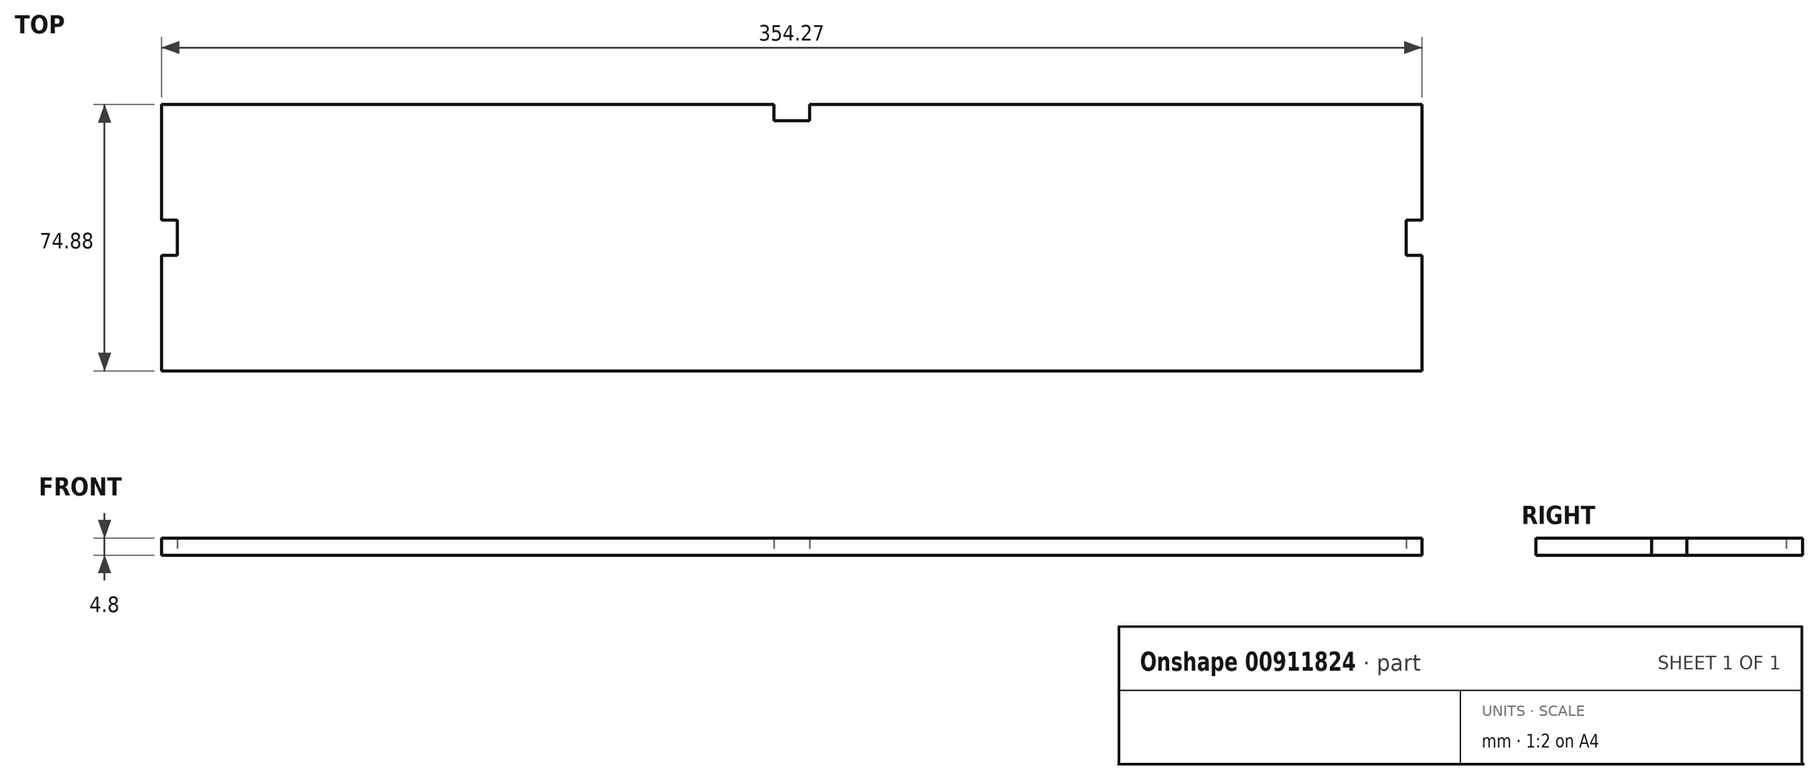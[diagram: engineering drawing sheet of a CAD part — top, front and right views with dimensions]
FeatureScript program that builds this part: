
annotation { "Feature Type Name" : "Feature", "Feature Type Description" : "" }
export const myFeature = defineFeature(function(context is Context, id is Id, definition is map)
    precondition{}
    {
        {
            var Q0;
            Q0=qCreatedBy(makeId("Top.planeOp"),FACE);
            var sketch = newSketch(context, id + "F0", { "sketchPlane" : qUnion([Q0])});
            skLineSegment(sketch, "E0.bottom", {"start": v(-87.1, 60.92) * mm, "end": v(85.03, 60.92) * mm});
            skLineSegment(sketch, "E0.top", {"start": v(-87.1, -13.96) * mm, "end": v(85.03, -13.96) * mm});
            skLineSegment(sketch, "E0.left", {"start": v(-87.1, 60.92) * mm, "end": v(-87.1, 28.48) * mm});
            skLineSegment(sketch, "E0.right", {"start": v(267.17, 60.92) * mm, "end": v(267.17, 28.48) * mm});
            skLineSegment(sketch, "E1", {"start": v(-82.6, 23.48) * mm, "end": v(262.67, 23.48) * mm});
            skLineSegment(sketch, "E2", {"start": v(90.03, 56.42) * mm, "end": v(90.03, -9.46) * mm});
            skLineSegment(sketch, "E3", {"start": v(-82.6, 23.48) * mm, "end": v(-82.6, 28.48) * mm});
            skLineSegment(sketch, "E4", {"start": v(-82.6, 28.48) * mm, "end": v(-87.1, 28.48) * mm});
            skLineSegment(sketch, "E5.MirrorCS", {"start": v(-82.6, 18.48) * mm, "end": v(-87.1, 18.48) * mm});
            skLineSegment(sketch, "E6.MirrorCS", {"start": v(-82.6, 23.48) * mm, "end": v(-82.6, 18.48) * mm});
            skLineSegment(sketch, "E7.MirrorCS", {"start": v(262.67, 28.48) * mm, "end": v(267.17, 28.48) * mm});
            skLineSegment(sketch, "E8.MirrorCS", {"start": v(262.67, 23.48) * mm, "end": v(262.67, 28.48) * mm});
            skLineSegment(sketch, "E9.MirrorCS", {"start": v(262.67, 18.48) * mm, "end": v(267.17, 18.48) * mm});
            skLineSegment(sketch, "E10.MirrorCS", {"start": v(262.67, 23.48) * mm, "end": v(262.67, 18.48) * mm});
            skLineSegment(sketch, "E11", {"start": v(90.03, 56.42) * mm, "end": v(95.03, 56.42) * mm});
            skLineSegment(sketch, "E12", {"start": v(95.03, 56.42) * mm, "end": v(95.03, 60.92) * mm});
            skLineSegment(sketch, "E13.MirrorCS", {"start": v(90.03, 56.42) * mm, "end": v(85.03, 56.42) * mm});
            skLineSegment(sketch, "E14.MirrorCS", {"start": v(85.03, 56.42) * mm, "end": v(85.03, 60.92) * mm});
            skLineSegment(sketch, "E15.trimOffspring", {"start": v(95.03, 60.92) * mm, "end": v(267.17, 60.92) * mm});
            skPoint(sketch, "E16.start.orphan", {"position": v(90.03, 60.92) * mm});
            skLineSegment(sketch, "E17.trimOffspring", {"start": v(-87.1, 18.48) * mm, "end": v(-87.1, -13.96) * mm});
            skPoint(sketch, "E18.start.orphan", {"position": v(-87.1, 23.48) * mm});
            skPoint(sketch, "E19.orphan", {"position": v(267.17, 23.48) * mm});
            skLineSegment(sketch, "E20.trimOffspring", {"start": v(267.17, 18.48) * mm, "end": v(267.17, -13.96) * mm});
            skPoint(sketch, "E21.MirrorP", {"position": v(90.03, -13.96) * mm});
            skLineSegment(sketch, "E22.MirrorCS", {"start": v(90.03, -9.46) * mm, "end": v(95.03, -9.46) * mm});
            skLineSegment(sketch, "E23.MirrorCS", {"start": v(90.03, -9.46) * mm, "end": v(85.03, -9.46) * mm});
            skLineSegment(sketch, "E24.MirrorCS", {"start": v(95.03, -9.46) * mm, "end": v(95.03, -13.96) * mm});
            skLineSegment(sketch, "E25.MirrorCS", {"start": v(85.03, -9.46) * mm, "end": v(85.03, -13.96) * mm});
            skLineSegment(sketch, "E26.trimOffspring", {"start": v(95.03, -13.96) * mm, "end": v(267.17, -13.96) * mm});
            skLineSegment(sketch, "E27", {"start": v(85.03, -13.96) * mm, "end": v(95.03, -13.96) * mm});
            skLineSegment(sketch, "E28", {"start": v(-92.1, 60.92) * mm, "end": v(-92.1, -13.96) * mm});
            skLineSegment(sketch, "E29", {"start": v(-92.1, -13.96) * mm, "end": v(-87.1, -13.96) * mm});
            skLineSegment(sketch, "E30", {"start": v(-87.1, 60.92) * mm, "end": v(-92.1, 60.92) * mm});
            skLineSegment(sketch, "E31", {"start": v(-87.1, 28.48) * mm, "end": v(-87.1, 18.48) * mm});
            skLineSegment(sketch, "E32", {"start": v(267.17, 60.92) * mm, "end": v(272.17, 60.92) * mm});
            skLineSegment(sketch, "E33", {"start": v(267.17, 28.48) * mm, "end": v(267.17, 18.48) * mm});
            skLineSegment(sketch, "E34", {"start": v(272.17, 60.92) * mm, "end": v(272.17, -13.96) * mm});
            skLineSegment(sketch, "E35", {"start": v(272.17, -13.96) * mm, "end": v(267.17, -13.96) * mm});
            skLineSegment(sketch, "E36", {"start": v(272.17, 60.92) * mm, "end": v(272.17, 65.92) * mm});
            skLineSegment(sketch, "E37", {"start": v(272.17, 65.92) * mm, "end": v(-92.1, 65.92) * mm});
            skLineSegment(sketch, "E38", {"start": v(-92.1, 65.92) * mm, "end": v(-92.1, 60.92) * mm});
            skLineSegment(sketch, "E39.MirrorCS", {"start": v(272.17, -18.96) * mm, "end": v(-92.1, -18.96) * mm});
            skLineSegment(sketch, "E40.MirrorCS", {"start": v(-92.1, -18.96) * mm, "end": v(-92.1, -13.96) * mm});
            skLineSegment(sketch, "E41.MirrorCS", {"start": v(272.17, -13.96) * mm, "end": v(272.17, -18.96) * mm});
            skLineSegment(sketch, "E42", {"start": v(85.03, 60.92) * mm, "end": v(95.03, 60.92) * mm});
            skSolve(sketch);
        }
        {
            var Q0;
            Q0=makeQuery(id+"F0.imprint","IMPRINT",FACE,{"disambiguationData":[TD([[makeQuery(id+"F0.imprint","IMPRINT",EDGE,{"derivedFrom":sQuery(id+"F0.wireOp",EDGE,"E0.top")}),1.0]])]});
            var Q1;
            Q1=makeQuery(id+"F0.imprint","IMPRINT",FACE,{"disambiguationData":[TD([[makeQuery(id+"F0.imprint","IMPRINT",EDGE,{"derivedFrom":sQuery(id+"F0.wireOp",EDGE,"E0.bottom")}),-1.0]])]});
            var Q2;
            Q2=makeQuery(id+"F0.imprint","IMPRINT",FACE,{"disambiguationData":[TD([[makeQuery(id+"F0.imprint","IMPRINT",EDGE,{"derivedFrom":sQuery(id+"F0.wireOp",EDGE,"E9.MirrorCS")}),-1.0]])]});
            var Q3;
            Q3=makeQuery(id+"F0.imprint","IMPRINT",FACE,{"disambiguationData":[TD([[makeQuery(id+"F0.imprint","IMPRINT",EDGE,{"derivedFrom":sQuery(id+"F0.wireOp",EDGE,"E0.right")}),-1.0]])]});
            var Q4;
            Q4=makeQuery(id+"F0.imprint","IMPRINT",FACE,{"disambiguationData":[TD([[makeQuery(id+"F0.imprint","IMPRINT",EDGE,{"derivedFrom":sQuery(id+"F0.wireOp",EDGE,"E22.MirrorCS")}),-1.0]])]});
            extrude(context, id + "F1", {"entities" : qUnion([Q0, Q1, Q2, Q3, Q4]), "depth" : 4.8 * mm, "offsetDistance" : 25 * mm});
        }
    });
